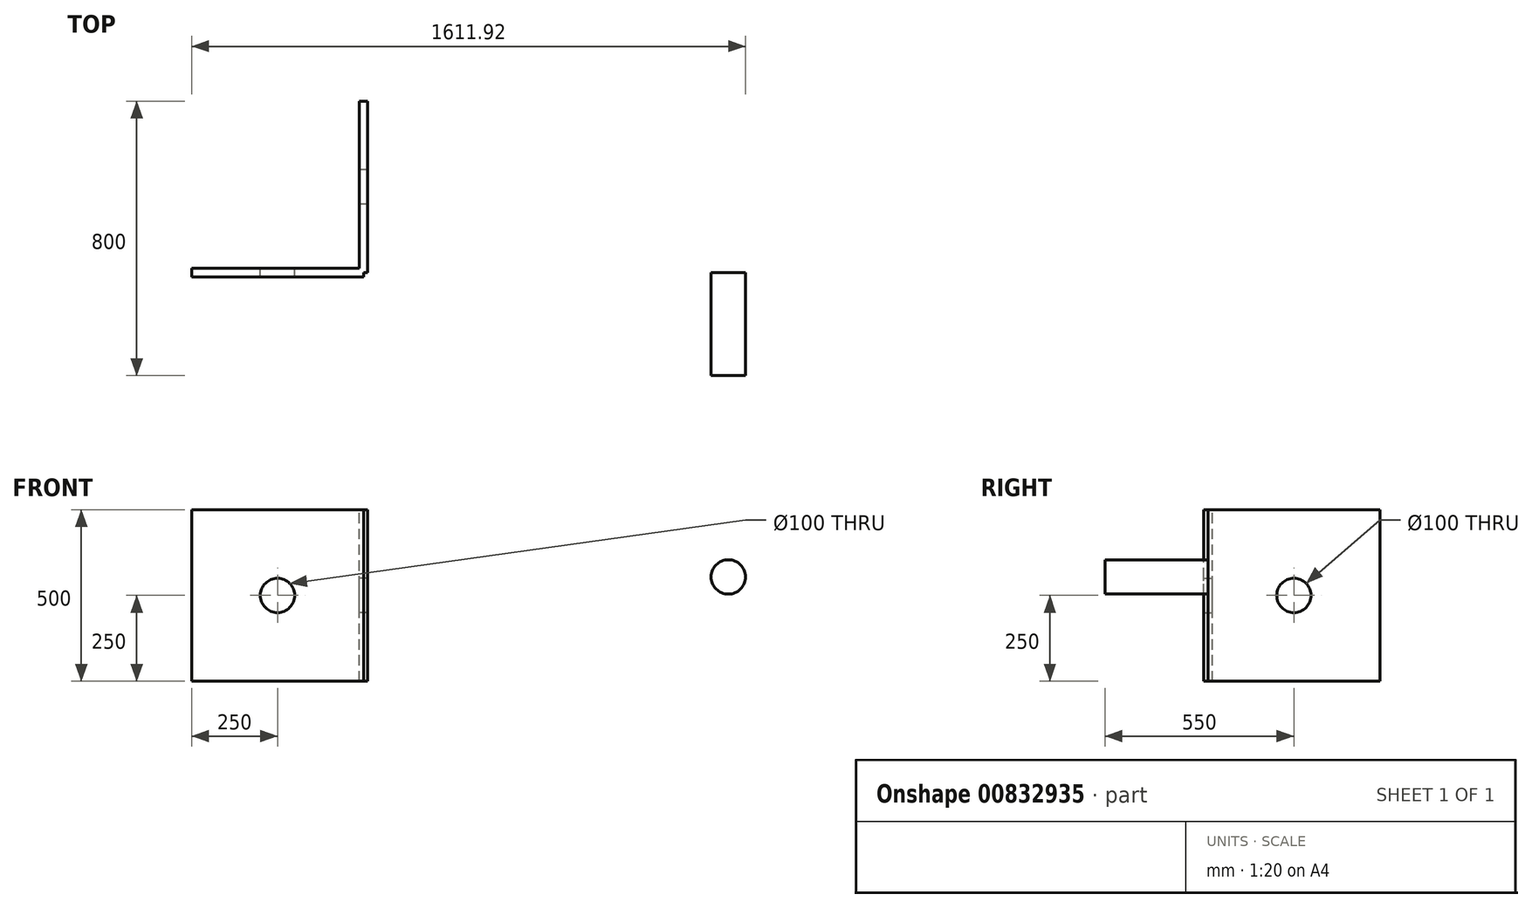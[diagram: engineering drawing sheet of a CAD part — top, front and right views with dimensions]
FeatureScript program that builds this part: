
annotation { "Feature Type Name" : "Feature", "Feature Type Description" : "" }
export const myFeature = defineFeature(function(context is Context, id is Id, definition is map)
    precondition{}
    {
        {
            var Q0;
            Q0=qCreatedBy(makeId("Front.planeOp"),FACE);
            var sketch = newSketch(context, id + "F0", { "sketchPlane" : qUnion([Q0])});
            skLineSegment(sketch, "E0.bottom", {"start": v(0, 0) * mm, "end": v(-500, 0) * mm});
            skLineSegment(sketch, "E0.top", {"start": v(0, 500) * mm, "end": v(-500, 500) * mm});
            skLineSegment(sketch, "E0.left", {"start": v(0, 0) * mm, "end": v(0, 500) * mm});
            skLineSegment(sketch, "E0.right", {"start": v(-500, 0) * mm, "end": v(-500, 500) * mm});
            skCircle(sketch, "E1", {"center": v(-250, 250) * mm, "radius": 50 * mm});
            skSolve(sketch);
        }
        {
            var Q0;
            Q0=makeQuery(id+"F0.imprint","IMPRINT",FACE,{"disambiguationData":[TD([[makeQuery(id+"F0.imprint","IMPRINT",EDGE,{"derivedFrom":sQuery(id+"F0.wireOp",EDGE,"E0.bottom")}),-1.0]])]});
            extrude(context, id + "F1", {"entities" : qUnion([Q0]), "endBound" : BoundingType.SYMMETRIC, "depth" : 25 * mm, "offsetDistance" : 25 * mm});
        }
        {
            var Q0;
            Q0=qCreatedBy(makeId("Right.planeOp"),FACE);
            var sketch = newSketch(context, id + "F2", { "sketchPlane" : qUnion([Q0])});
            skLineSegment(sketch, "E2.bottom", {"start": v(0, 0) * mm, "end": v(500, 0) * mm});
            skLineSegment(sketch, "E2.top", {"start": v(0, 500) * mm, "end": v(500, 500) * mm});
            skLineSegment(sketch, "E2.left", {"start": v(0, 0) * mm, "end": v(0, 500) * mm});
            skLineSegment(sketch, "E2.right", {"start": v(500, 0) * mm, "end": v(500, 500) * mm});
            skCircle(sketch, "E3", {"center": v(250, 250) * mm, "radius": 50 * mm});
            skSolve(sketch);
        }
        {
            var Q0;
            Q0=makeQuery(id+"F2.imprint","IMPRINT",FACE,{"disambiguationData":[TD([[makeQuery(id+"F2.imprint","IMPRINT",EDGE,{"derivedFrom":sQuery(id+"F2.wireOp",EDGE,"E2.bottom")}),1.0]])]});
            extrude(context, id + "F3", {"entities" : qUnion([Q0]), "operationType" : NewBodyOperationType.ADD, "endBound" : BoundingType.SYMMETRIC, "depth" : 25 * mm, "offsetDistance" : 25 * mm});
        }
        {
            var Q0;
            Q0=qCreatedBy(makeId("Front.planeOp"),FACE);
            var sketch = newSketch(context, id + "F4", { "sketchPlane" : qUnion([Q0])});
            skCircle(sketch, "E4", {"center": v(1061.92, 303.9) * mm, "radius": 50 * mm});
            skSolve(sketch);
        }
        {
            var Q0;
            Q0 = qSketchRegion(id + "F4", true);
            extrude(context, id + "F5", {"entities" : qUnion([Q0]), "depth" : 300 * mm, "offsetDistance" : 25 * mm});
        }
    });
